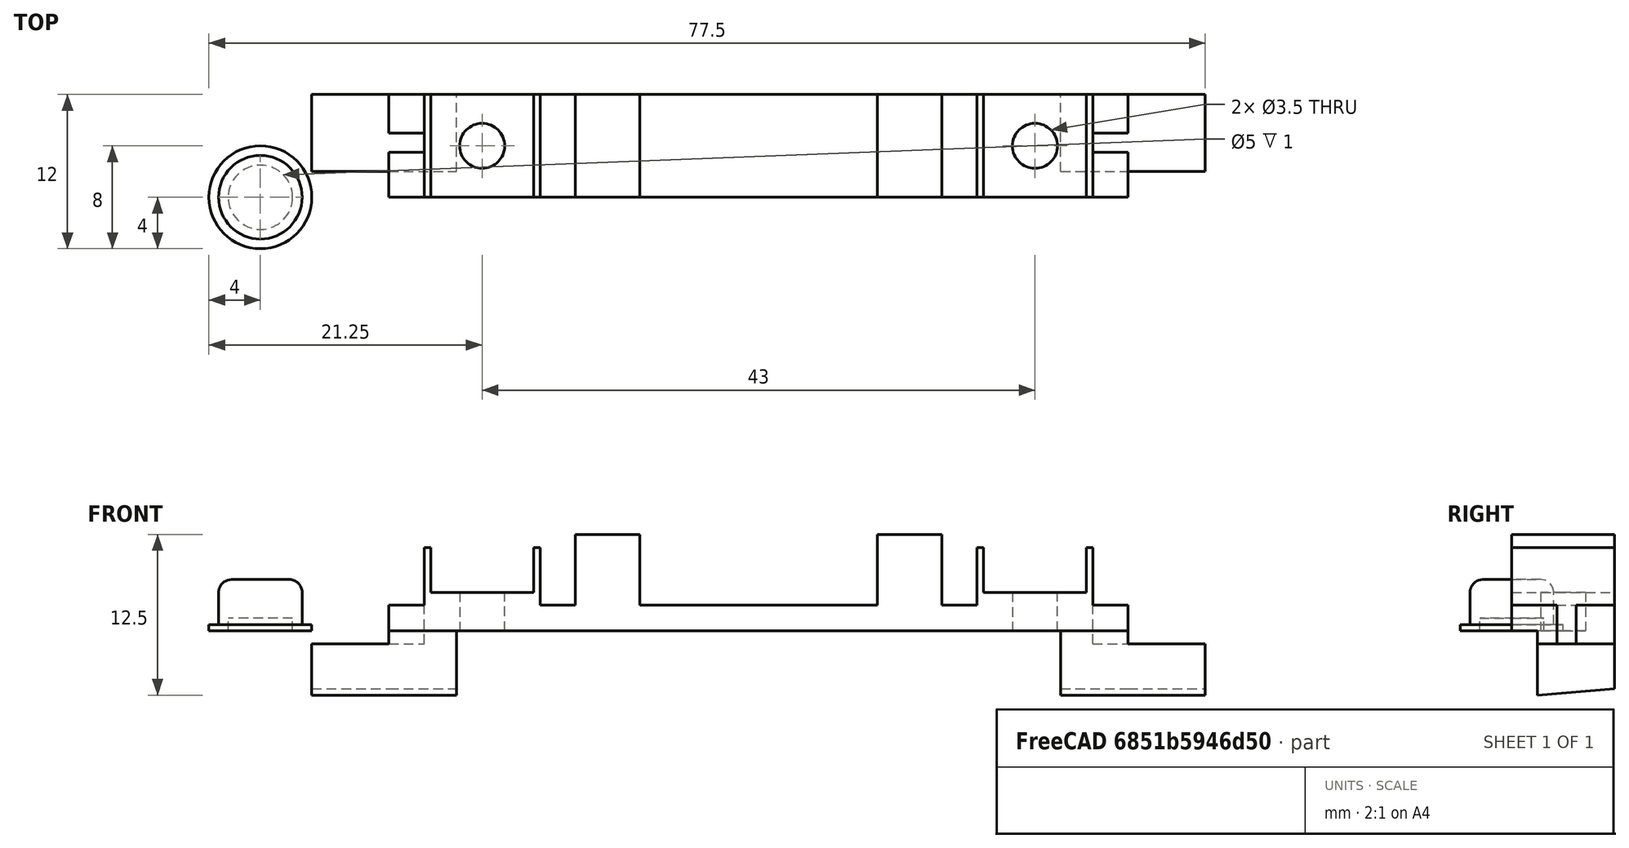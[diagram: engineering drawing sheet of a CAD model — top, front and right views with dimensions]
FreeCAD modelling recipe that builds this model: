
FCSTD DOCUMENT  (FreeCAD 1.0R38642 (Git))
Label: GBC_zero_L_R
License: All rights reserved
LicenseURL: http://en.wikipedia.org/wiki/All_rights_reserved
objects: Part::Box×9, Part::Cylinder×5, Part::Cut×4, Part::Wedge×4, Part::MultiFuse×3, Part::Fillet×1
note: 26 computed .brp shape members not serialized (recipe doc carries the construction recipe); baked Part::Feature solids carry a one-line shape summary decoded from their .brp

FEATURE [Part::Box] Box  label="Cube(back_board)"
  AttacherType = Attacher::AttachEngine3D
  Height = 2
  Length = 57.5
  Width = 8
FEATURE [Part::Box] Box001  label="Cube001(L_outer)"
  AttacherType = Attacher::AttachEngine3D
  Height = 4.5
  Length = 9
  Placement = pos=(2.75,0,2) rot=(0,0,1;0rad)
  Width = 8
FEATURE [Part::Box] Box003  label="Cube002(cutout_left)"
  AttacherType = Attacher::AttachEngine3D
  Height = 3
  Length = 2.75
  Placement = pos=(0,3.5,-1) rot=(0,0,1;0rad)
  Width = 1.5
FEATURE [Part::Box] Box004  label="Cube003(cutout_right)"
  AttacherType = Attacher::AttachEngine3D
  Height = 3
  Length = 2.75
  Placement = pos=(54.75,3.5,-1) rot=(0,0,1;0rad)
  Width = 1.5
FEATURE [Part::Box] Box005  label="Cube001(R_outer)"
  AttacherType = Attacher::AttachEngine3D
  Height = 4.5
  Length = 9
  Placement = pos=(45.75,0,2) rot=(0,0,1;0rad)
  Width = 8
FEATURE [Part::Box] Box006  label="Cube001(L_inner)"
  AttacherType = Attacher::AttachEngine3D
  Height = 3.5
  Length = 8
  Placement = pos=(3.25,0,3) rot=(0,0,1;0rad)
  Width = 8
FEATURE [Part::Box] Box007  label="Cube001(R_inner)"
  AttacherType = Attacher::AttachEngine3D
  Height = 3.5
  Length = 8
  Placement = pos=(46.25,0,3) rot=(0,0,1;0rad)
  Width = 8
FEATURE [Part::Cylinder] Cylinder  label="Cylinder(left)"
  Angle = 360
  AttacherType = Attacher::AttachEngine3D
  FirstAngle = 0
  Height = 5.5
  Placement = pos=(50.25,4,0) rot=(0,0,1;0rad)
  Radius = 1.75
  SecondAngle = 0
FEATURE [Part::Cylinder] Cylinder001  label="Cylinder(right)"
  Angle = 360
  AttacherType = Attacher::AttachEngine3D
  FirstAngle = 0
  Height = 5.5
  Placement = pos=(7.25,4,0) rot=(0,0,1;0rad)
  Radius = 1.75
  SecondAngle = 0
FEATURE [Part::Cylinder] Cylinder002  label="Cylinder(button_outer)"
  Angle = 360
  AttacherType = Attacher::AttachEngine3D
  FirstAngle = 0
  Height = 4
  Placement = pos=(-10,0,0) rot=(0,0,1;0rad)
  Radius = 3.25
  SecondAngle = 0
FEATURE [Part::Cylinder] Cylinder003  label="Cylinder001(rim)"
  Angle = 360
  AttacherType = Attacher::AttachEngine3D
  FirstAngle = 0
  Height = 0.5
  Placement = pos=(-10,0,0) rot=(0,0,1;0rad)
  Radius = 4
  SecondAngle = 0
FEATURE [Part::Cylinder] Cylinder004  label="Cylinder001(button_inner)"
  Angle = 360
  AttacherType = Attacher::AttachEngine3D
  FirstAngle = 0
  Height = 1
  Placement = pos=(-10,0,0) rot=(0,0,1;0rad)
  Radius = 2.5
  SecondAngle = 0
FEATURE [Part::MultiFuse] Fusion001
  Shapes = -> [Cylinder002,Cylinder003]
FEATURE [Part::Cut] Cut006
  Base = -> Fusion001
  Tool = -> Cylinder004
FEATURE [Part::Box] Box009  label="Cube(left_front_block)"
  AttacherType = Attacher::AttachEngine3D
  Height = 5.5
  Length = 5
  Placement = pos=(38,0,2) rot=(0,0,1;0rad)
  Width = 8
FEATURE [Part::Box] Box010  label="Cube001(right_front_block)"
  AttacherType = Attacher::AttachEngine3D
  Height = 5.5
  Length = 5
  Placement = pos=(14.5,0,2) rot=(0,0,1;0rad)
  Width = 8
FEATURE [Part::Fillet] Fillet  label="Fillet(button)"
  Base = -> Cut006
  EdgeLinks = -> Cut006 [Edge3]
  Edges = 1 edges r=1: [Edge3]
FEATURE [Part::Wedge] Wedge  label="Wedge(right)"
  AttacherType = Attacher::AttachEngine3D
  Placement = pos=(0,2,0) rot=(0,1,0;1.5708rad)
  X2max = 4.5
  X2min = 0
  Xmax = 5
  Xmin = 0
  Ymax = 6
  Ymin = 0
  Z2max = 5.25
  Z2min = 0
  Zmax = 5.25
  Zmin = 0
FEATURE [Part::Wedge] Wedge001  label="Wedge001(left)"
  AttacherType = Attacher::AttachEngine3D
  Placement = pos=(52.25,2,0) rot=(0,1,0;1.5708rad)
  X2max = 4.5
  X2min = 0
  Xmax = 5
  Xmin = 0
  Ymax = 6
  Ymin = 0
  Z2max = 5.25
  Z2min = 0
  Zmax = 5.25
  Zmin = 0
FEATURE [Part::Wedge] Wedge002  label="Wedge(right)001"
  AttacherType = Attacher::AttachEngine3D
  Placement = pos=(-6,2,-1) rot=(0,1,0;1.5708rad)
  X2max = 3.5
  X2min = 0
  Xmax = 4
  Xmin = 0
  Ymax = 6
  Ymin = 0
  Z2max = 6
  Z2min = 0
  Zmax = 6
  Zmin = 0
FEATURE [Part::Wedge] Wedge003  label="Wedge001(left)001"
  AttacherType = Attacher::AttachEngine3D
  Placement = pos=(57.5,2,-1) rot=(0,1,0;1.5708rad)
  X2max = 3.5
  X2min = 0
  Xmax = 4
  Xmin = 0
  Ymax = 6
  Ymin = 0
  Z2max = 6
  Z2min = 0
  Zmax = 6
  Zmin = 0
FEATURE [Part::Cut] Cut
  Base = -> Box001
  Tool = -> Box006
FEATURE [Part::Cut] Cut007
  Base = -> Box005
  Tool = -> Box007
FEATURE [Part::MultiFuse] Fusion
  Shapes = -> [Box009,Box010,Wedge,Wedge001,Wedge002,Wedge003,Box,Cut,Cut007]
FEATURE [Part::MultiFuse] Fusion002
  Shapes = -> [Box003,Box004,Cylinder,Cylinder001]
FEATURE [Part::Cut] Cut008  label="Cut008(braket)"
  Base = -> Fusion
  Tool = -> Fusion002
